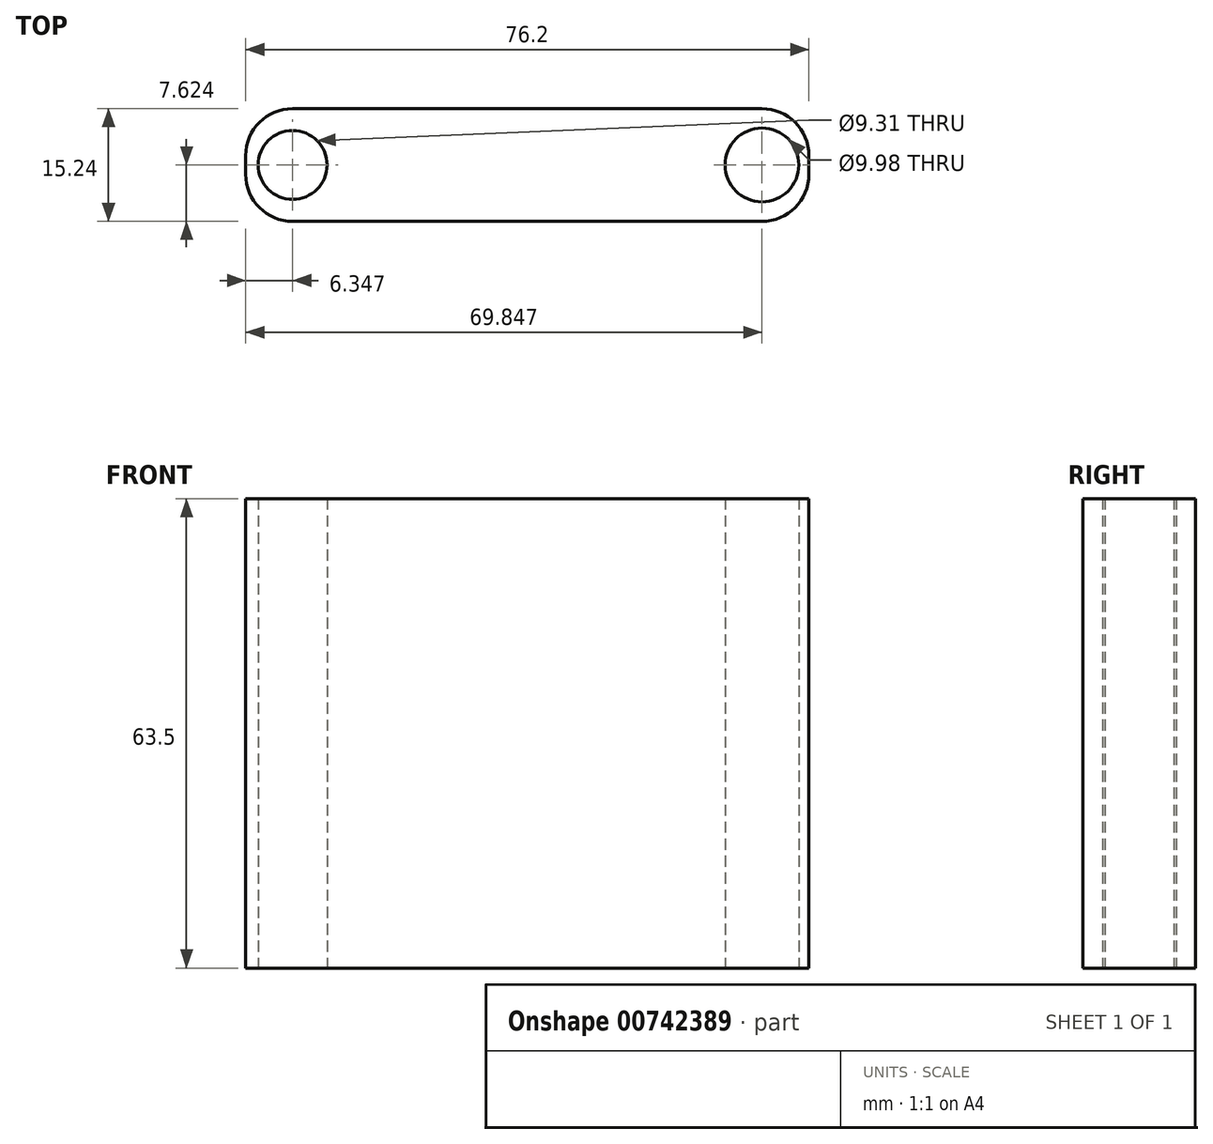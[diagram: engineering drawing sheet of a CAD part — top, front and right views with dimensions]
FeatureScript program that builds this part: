
annotation { "Feature Type Name" : "Feature", "Feature Type Description" : "" }
export const myFeature = defineFeature(function(context is Context, id is Id, definition is map)
    precondition{}
    {
        {
            var Q0;
            Q0=qCreatedBy(makeId("Top.planeOp"),FACE);
            var sketch = newSketch(context, id + "F0", { "sketchPlane" : qUnion([Q0])});
            skLineSegment(sketch, "E0", {"start": v(-51.64, 12.8) * mm, "end": v(11.86, 12.8) * mm});
            skLineSegment(sketch, "E1", {"start": v(18.2, 6.46) * mm, "end": v(18.2, 3.92) * mm});
            skLineSegment(sketch, "E2", {"start": v(11.86, -2.43) * mm, "end": v(-51.64, -2.43) * mm});
            skLineSegment(sketch, "E3", {"start": v(-58, 3.92) * mm, "end": v(-58, 6.46) * mm});
            skPoint(sketch, "E4.visualSharp", {"position": v(-58, 12.8) * mm});
            skArc(sketch, "E4.filletArc", {"start": v(-51.64, 12.8) * mm, "mid": v(-56.13, 10.95) * mm, "end": v(-58, 6.46) * mm});
            skPoint(sketch, "E5.visualSharp", {"position": v(-58, -2.43) * mm});
            skArc(sketch, "E5.filletArc", {"start": v(-58, 3.92) * mm, "mid": v(-56.13, -0.57) * mm, "end": v(-51.64, -2.43) * mm});
            skPoint(sketch, "E6.visualSharp", {"position": v(18.2, 12.8) * mm});
            skArc(sketch, "E6.filletArc", {"start": v(18.2, 6.46) * mm, "mid": v(16.35, 10.95) * mm, "end": v(11.86, 12.8) * mm});
            skPoint(sketch, "E7.visualSharp", {"position": v(18.2, -2.43) * mm});
            skArc(sketch, "E7.filletArc", {"start": v(11.86, -2.43) * mm, "mid": v(16.35, -0.57) * mm, "end": v(18.2, 3.92) * mm});
            skCircle(sketch, "E8", {"center": v(-51.64, 5.2) * mm, "radius": 4.66 * mm});
            skCircle(sketch, "E9", {"center": v(11.86, 5.2) * mm, "radius": 4.99 * mm});
            skSolve(sketch);
        }
        {
            var Q0;
            Q0 = qSketchRegion(id + "F0", true);
            extrude(context, id + "F1", {"entities" : qUnion([Q0]), "depth" : 63.5 * mm, "offsetDistance" : 25.4 * mm});
        }
    });
